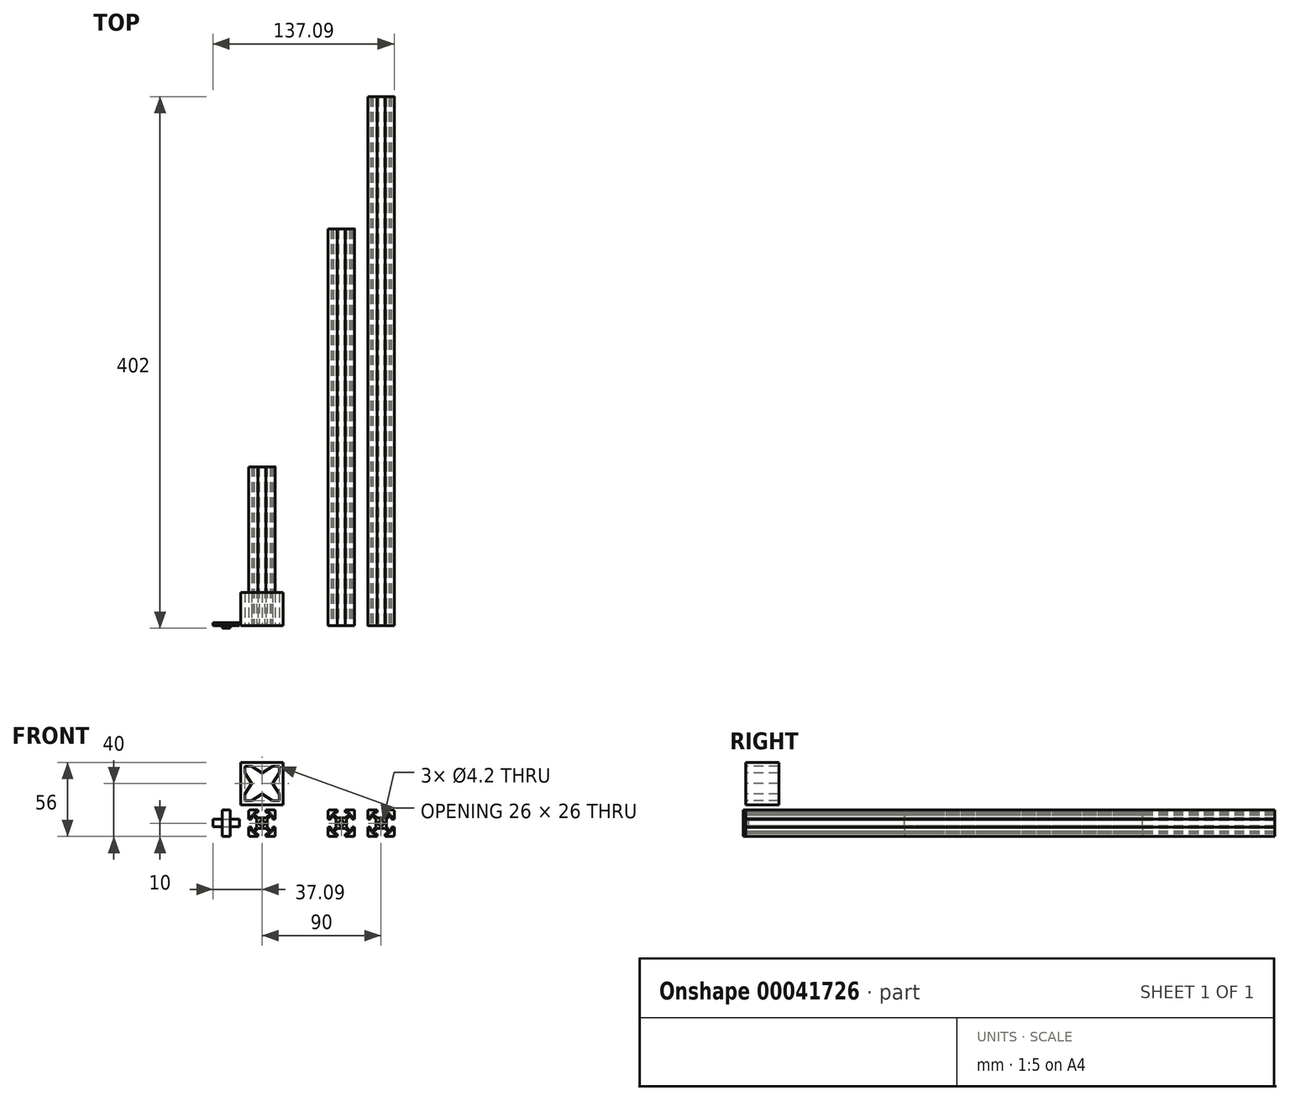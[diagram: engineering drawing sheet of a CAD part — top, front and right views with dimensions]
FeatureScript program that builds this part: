
annotation { "Feature Type Name" : "Feature", "Feature Type Description" : "" }
export const myFeature = defineFeature(function(context is Context, id is Id, definition is map)
    precondition{}
    {
        {
            var Q0;
            Q0=qCreatedBy(makeId("Front.planeOp"),FACE);
            var sketch = newSketch(context, id + "F0", { "sketchPlane" : qUnion([Q0])});
            skLineSegment(sketch, "E0", {"start": v(0, 4) * mm, "end": v(3, 4) * mm});
            skLineSegment(sketch, "E1", {"start": v(3, 4) * mm, "end": v(6, 7) * mm});
            skLineSegment(sketch, "E2", {"start": v(6, 7) * mm, "end": v(6, 8) * mm});
            skLineSegment(sketch, "E3", {"start": v(6, 8) * mm, "end": v(3, 8) * mm});
            skLineSegment(sketch, "E4", {"start": v(3, 8) * mm, "end": v(3, 10) * mm});
            skLineSegment(sketch, "E5", {"start": v(3, 10) * mm, "end": v(9, 10) * mm});
            skLineSegment(sketch, "E6", {"start": v(0, 0) * mm, "end": v(12.93, 12.93) * mm, "construction": true});
            skLineSegment(sketch, "E7.MirrorCS", {"start": v(4, 0) * mm, "end": v(4, 3) * mm});
            skLineSegment(sketch, "E8.MirrorCS", {"start": v(10, 3) * mm, "end": v(10, 9) * mm});
            skLineSegment(sketch, "E9.MirrorCS", {"start": v(8, 3) * mm, "end": v(10, 3) * mm});
            skLineSegment(sketch, "E10.MirrorCS", {"start": v(8, 6) * mm, "end": v(8, 3) * mm});
            skLineSegment(sketch, "E11.MirrorCS", {"start": v(4, 3) * mm, "end": v(7, 6) * mm});
            skLineSegment(sketch, "E12.MirrorCS", {"start": v(7, 6) * mm, "end": v(8, 6) * mm});
            skLineSegment(sketch, "E13.MirrorCS", {"start": v(-8, 3) * mm, "end": v(-10, 3) * mm});
            skLineSegment(sketch, "E14.MirrorCS", {"start": v(0, 4) * mm, "end": v(-3, 4) * mm});
            skLineSegment(sketch, "E15.MirrorCS", {"start": v(-3, 4) * mm, "end": v(-6, 7) * mm});
            skLineSegment(sketch, "E16.MirrorCS", {"start": v(-6, 7) * mm, "end": v(-6, 8) * mm});
            skLineSegment(sketch, "E17.MirrorCS", {"start": v(-6, 8) * mm, "end": v(-3, 8) * mm});
            skLineSegment(sketch, "E18.MirrorCS", {"start": v(-3, 8) * mm, "end": v(-3, 10) * mm});
            skLineSegment(sketch, "E19.MirrorCS", {"start": v(-3, 10) * mm, "end": v(-9, 10) * mm});
            skLineSegment(sketch, "E20.MirrorCS", {"start": v(-4, 0) * mm, "end": v(-4, 3) * mm});
            skLineSegment(sketch, "E21.MirrorCS", {"start": v(-10, 3) * mm, "end": v(-10, 9) * mm});
            skLineSegment(sketch, "E22.MirrorCS", {"start": v(-8, 6) * mm, "end": v(-8, 3) * mm});
            skLineSegment(sketch, "E23.MirrorCS", {"start": v(-4, 3) * mm, "end": v(-7, 6) * mm});
            skLineSegment(sketch, "E24.MirrorCS", {"start": v(-7, 6) * mm, "end": v(-8, 6) * mm});
            skLineSegment(sketch, "E25.MirrorCS", {"start": v(-7, -6) * mm, "end": v(-8, -6) * mm});
            skLineSegment(sketch, "E26.MirrorCS", {"start": v(-6, -7) * mm, "end": v(-6, -8) * mm});
            skLineSegment(sketch, "E27.MirrorCS", {"start": v(6, -7) * mm, "end": v(6, -8) * mm});
            skLineSegment(sketch, "E28.MirrorCS", {"start": v(7, -6) * mm, "end": v(8, -6) * mm});
            skLineSegment(sketch, "E29.MirrorCS", {"start": v(8, -3) * mm, "end": v(10, -3) * mm});
            skLineSegment(sketch, "E30.MirrorCS", {"start": v(-8, -3) * mm, "end": v(-10, -3) * mm});
            skLineSegment(sketch, "E31.MirrorCS", {"start": v(-6, -8) * mm, "end": v(-3, -8) * mm});
            skLineSegment(sketch, "E32.MirrorCS", {"start": v(-3, -10) * mm, "end": v(-9, -10) * mm});
            skLineSegment(sketch, "E33.MirrorCS", {"start": v(-4, -3) * mm, "end": v(-7, -6) * mm});
            skLineSegment(sketch, "E34.MirrorCS", {"start": v(-4, 0) * mm, "end": v(-4, -3) * mm});
            skLineSegment(sketch, "E35.MirrorCS", {"start": v(-3, -8) * mm, "end": v(-3, -10) * mm});
            skLineSegment(sketch, "E36.MirrorCS", {"start": v(0, -4) * mm, "end": v(-3, -4) * mm});
            skLineSegment(sketch, "E37.MirrorCS", {"start": v(0, -4) * mm, "end": v(3, -4) * mm});
            skLineSegment(sketch, "E38.MirrorCS", {"start": v(6, -8) * mm, "end": v(3, -8) * mm});
            skLineSegment(sketch, "E39.MirrorCS", {"start": v(3, -8) * mm, "end": v(3, -10) * mm});
            skLineSegment(sketch, "E40.MirrorCS", {"start": v(3, -10) * mm, "end": v(9, -10) * mm});
            skLineSegment(sketch, "E41.MirrorCS", {"start": v(3, -4) * mm, "end": v(6, -7) * mm});
            skLineSegment(sketch, "E42.MirrorCS", {"start": v(-3, -4) * mm, "end": v(-6, -7) * mm});
            skLineSegment(sketch, "E43.MirrorCS", {"start": v(4, 0) * mm, "end": v(4, -3) * mm});
            skLineSegment(sketch, "E44.MirrorCS", {"start": v(10, -3) * mm, "end": v(10, -9) * mm});
            skLineSegment(sketch, "E45.MirrorCS", {"start": v(8, -6) * mm, "end": v(8, -3) * mm});
            skLineSegment(sketch, "E46.MirrorCS", {"start": v(4, -3) * mm, "end": v(7, -6) * mm});
            skLineSegment(sketch, "E47.MirrorCS", {"start": v(-8, -6) * mm, "end": v(-8, -3) * mm});
            skLineSegment(sketch, "E48.MirrorCS", {"start": v(-10, -3) * mm, "end": v(-10, -9) * mm});
            skCircle(sketch, "E49", {"center": v(0, 0) * mm, "radius": 2.1 * mm});
            skPoint(sketch, "E50.visualSharp", {"position": v(-10, 10) * mm});
            skArc(sketch, "E50.filletArc", {"start": v(-9, 10) * mm, "mid": v(-9.7, 9.7) * mm, "end": v(-10, 9) * mm});
            skPoint(sketch, "E51.visualSharp", {"position": v(10, 10) * mm});
            skArc(sketch, "E51.filletArc", {"start": v(10, 9) * mm, "mid": v(9.7, 9.7) * mm, "end": v(9, 10) * mm});
            skPoint(sketch, "E52.visualSharp", {"position": v(10, -10) * mm});
            skArc(sketch, "E52.filletArc", {"start": v(9, -10) * mm, "mid": v(9.7, -9.7) * mm, "end": v(10, -9) * mm});
            skPoint(sketch, "E53.visualSharp", {"position": v(-10, -10) * mm});
            skArc(sketch, "E53.filletArc", {"start": v(-10, -9) * mm, "mid": v(-9.7, -9.7) * mm, "end": v(-9, -10) * mm});
            skLineSegment(sketch, "E54", {"start": v(-3, 4) * mm, "end": v(-3, 8) * mm, "construction": true});
            skLineSegment(sketch, "E55", {"start": v(3, 4) * mm, "end": v(3, 8) * mm, "construction": true});
            skSolve(sketch);
        }
        {
            var Q0;
            Q0=makeQuery(id+"F0.imprint","IMPRINT",FACE,{"disambiguationData":[TD([[makeQuery(id+"F0.imprint","IMPRINT",EDGE,{"derivedFrom":sQuery(id+"F0.wireOp",EDGE,"E0")}),-1.0]])]});
            extrude(context, id + "F1", {"entities" : qUnion([Q0]), "oppositeDirection" : true, "depth" : 120 * mm});
        }
        {
            var Q0;
            Q0=makeQuery(id+"F0.imprint","IMPRINT",FACE,{"disambiguationData":[TD([[makeQuery(id+"F0.imprint","IMPRINT",EDGE,{"derivedFrom":sQuery(id+"F0.wireOp",EDGE,"E0")}),-1.0]])]});
            var sketch = newSketch(context, id + "F2", { "sketchPlane" : qUnion([Q0])});
            skLineSegment(sketch, "E56.0", {"start": v(0, 0) * mm, "end": v(12.93, 12.93) * mm, "construction": true});
            skLineSegment(sketch, "E57", {"start": v(13, 13) * mm, "end": v(7.97, 13) * mm});
            skLineSegment(sketch, "E58", {"start": v(7.97, 13) * mm, "end": v(0, 8) * mm});
            skLineSegment(sketch, "E59.MirrorCS", {"start": v(13, 13) * mm, "end": v(13, 7.97) * mm});
            skLineSegment(sketch, "E60.MirrorCS", {"start": v(13, 7.97) * mm, "end": v(8, 0) * mm});
            skLineSegment(sketch, "E61.MirrorCS", {"start": v(-7.97, 13) * mm, "end": v(0, 8) * mm});
            skLineSegment(sketch, "E62.MirrorCS", {"start": v(-13, 13) * mm, "end": v(-7.97, 13) * mm});
            skLineSegment(sketch, "E63.MirrorCS", {"start": v(-13, 7.97) * mm, "end": v(-8, 0) * mm});
            skLineSegment(sketch, "E64.MirrorCS", {"start": v(-13, 13) * mm, "end": v(-13, 7.97) * mm});
            skLineSegment(sketch, "E65.MirrorCS", {"start": v(-7.97, -13) * mm, "end": v(0, -8) * mm});
            skLineSegment(sketch, "E66.MirrorCS", {"start": v(-13, -13) * mm, "end": v(-7.97, -13) * mm});
            skLineSegment(sketch, "E67.MirrorCS", {"start": v(7.97, -13) * mm, "end": v(0, -8) * mm});
            skLineSegment(sketch, "E68.MirrorCS", {"start": v(-13, -7.97) * mm, "end": v(-8, 0) * mm});
            skLineSegment(sketch, "E69.MirrorCS", {"start": v(-13, -13) * mm, "end": v(-13, -7.97) * mm});
            skLineSegment(sketch, "E70.MirrorCS", {"start": v(13, -13) * mm, "end": v(7.97, -13) * mm});
            skLineSegment(sketch, "E71.MirrorCS", {"start": v(13, -13) * mm, "end": v(13, -7.97) * mm});
            skLineSegment(sketch, "E72.MirrorCS", {"start": v(13, -7.97) * mm, "end": v(8, 0) * mm});
            skLineSegment(sketch, "E73.rect.bottom", {"start": v(-16, 16) * mm, "end": v(16, 16) * mm});
            skLineSegment(sketch, "E73.rect.top", {"start": v(-16, -16) * mm, "end": v(16, -16) * mm});
            skLineSegment(sketch, "E73.rect.left", {"start": v(-16, 16) * mm, "end": v(-16, -16) * mm});
            skLineSegment(sketch, "E73.rect.right", {"start": v(16, 16) * mm, "end": v(16, -16) * mm});
            skPoint(sketch, "E73.rect.middle", {"position": v(0, 0) * mm});
            skSolve(sketch);
        }
        {
            var Q0;
            Q0=qSketchRegion(id+"F0",true);
            extrude(context, id + "F3", {"entities" : qUnion([Q0]), "oppositeDirection" : true, "depth" : 300 * mm});
        }
        {
            var Q0;
            Q0=qSketchRegion(id+"F0",true);
            extrude(context, id + "F4", {"entities" : qUnion([Q0]), "oppositeDirection" : true, "depth" : 400 * mm});
        }
        {
            var Q0;
            Q0=makeQuery(id+"F3.opExtrude","SWEPT_BODY",BODY,{"disambiguationData":[OSD([sQuery(id+"F0.wireOp",EDGE,"E0"),sQuery(id+"F0.wireOp",EDGE,"E1"),sQuery(id+"F0.wireOp",EDGE,"E2"),sQuery(id+"F0.wireOp",EDGE,"E3"),sQuery(id+"F0.wireOp",EDGE,"E4"),sQuery(id+"F0.wireOp",EDGE,"E5"),sQuery(id+"F0.wireOp",EDGE,"E7.MirrorCS"),sQuery(id+"F0.wireOp",EDGE,"E8.MirrorCS"),sQuery(id+"F0.wireOp",EDGE,"E10.MirrorCS"),sQuery(id+"F0.wireOp",EDGE,"E11.MirrorCS"),sQuery(id+"F0.wireOp",EDGE,"E12.MirrorCS"),sQuery(id+"F0.wireOp",EDGE,"E9.MirrorCS"),sQuery(id+"F0.wireOp",EDGE,"E14.MirrorCS"),sQuery(id+"F0.wireOp",EDGE,"E15.MirrorCS"),sQuery(id+"F0.wireOp",EDGE,"E16.MirrorCS"),sQuery(id+"F0.wireOp",EDGE,"E17.MirrorCS"),sQuery(id+"F0.wireOp",EDGE,"E18.MirrorCS"),sQuery(id+"F0.wireOp",EDGE,"E19.MirrorCS"),sQuery(id+"F0.wireOp",EDGE,"E20.MirrorCS"),sQuery(id+"F0.wireOp",EDGE,"E21.MirrorCS"),sQuery(id+"F0.wireOp",EDGE,"E22.MirrorCS"),sQuery(id+"F0.wireOp",EDGE,"E23.MirrorCS"),sQuery(id+"F0.wireOp",EDGE,"E13.MirrorCS"),sQuery(id+"F0.wireOp",EDGE,"E24.MirrorCS"),sQuery(id+"F0.wireOp",EDGE,"E25.MirrorCS"),sQuery(id+"F0.wireOp",EDGE,"E26.MirrorCS"),sQuery(id+"F0.wireOp",EDGE,"E27.MirrorCS"),sQuery(id+"F0.wireOp",EDGE,"E28.MirrorCS"),sQuery(id+"F0.wireOp",EDGE,"E31.MirrorCS"),sQuery(id+"F0.wireOp",EDGE,"E32.MirrorCS"),sQuery(id+"F0.wireOp",EDGE,"E33.MirrorCS"),sQuery(id+"F0.wireOp",EDGE,"E34.MirrorCS"),sQuery(id+"F0.wireOp",EDGE,"E35.MirrorCS"),sQuery(id+"F0.wireOp",EDGE,"E36.MirrorCS"),sQuery(id+"F0.wireOp",EDGE,"E37.MirrorCS"),sQuery(id+"F0.wireOp",EDGE,"E38.MirrorCS"),sQuery(id+"F0.wireOp",EDGE,"E39.MirrorCS"),sQuery(id+"F0.wireOp",EDGE,"E40.MirrorCS"),sQuery(id+"F0.wireOp",EDGE,"E41.MirrorCS"),sQuery(id+"F0.wireOp",EDGE,"E42.MirrorCS"),sQuery(id+"F0.wireOp",EDGE,"E43.MirrorCS"),sQuery(id+"F0.wireOp",EDGE,"E44.MirrorCS"),sQuery(id+"F0.wireOp",EDGE,"E29.MirrorCS"),sQuery(id+"F0.wireOp",EDGE,"E45.MirrorCS"),sQuery(id+"F0.wireOp",EDGE,"E46.MirrorCS"),sQuery(id+"F0.wireOp",EDGE,"E47.MirrorCS"),sQuery(id+"F0.wireOp",EDGE,"E48.MirrorCS"),sQuery(id+"F0.wireOp",EDGE,"E30.MirrorCS"),sQuery(id+"F0.wireOp",EDGE,"E49"),sQuery(id+"F0.wireOp",EDGE,"E50.filletArc"),sQuery(id+"F0.wireOp",EDGE,"E51.filletArc"),sQuery(id+"F0.wireOp",EDGE,"E52.filletArc"),sQuery(id+"F0.wireOp",EDGE,"E53.filletArc")])]});
            transform(context, id + "F5", {"entities" : qUnion([Q0]), "transformType" : TransformType.TRANSLATION_3D, "dx" : 60 * mm, "dy" : 0 * mm, "dz" : 0 * mm, "makeCopy" : false});
        }
        {
            var Q0;
            Q0=makeQuery(id+"F4.opExtrude","SWEPT_BODY",BODY,{"disambiguationData":[OSD([sQuery(id+"F0.wireOp",EDGE,"E0"),sQuery(id+"F0.wireOp",EDGE,"E1"),sQuery(id+"F0.wireOp",EDGE,"E2"),sQuery(id+"F0.wireOp",EDGE,"E3"),sQuery(id+"F0.wireOp",EDGE,"E4"),sQuery(id+"F0.wireOp",EDGE,"E5"),sQuery(id+"F0.wireOp",EDGE,"E7.MirrorCS"),sQuery(id+"F0.wireOp",EDGE,"E8.MirrorCS"),sQuery(id+"F0.wireOp",EDGE,"E10.MirrorCS"),sQuery(id+"F0.wireOp",EDGE,"E11.MirrorCS"),sQuery(id+"F0.wireOp",EDGE,"E12.MirrorCS"),sQuery(id+"F0.wireOp",EDGE,"E9.MirrorCS"),sQuery(id+"F0.wireOp",EDGE,"E14.MirrorCS"),sQuery(id+"F0.wireOp",EDGE,"E15.MirrorCS"),sQuery(id+"F0.wireOp",EDGE,"E16.MirrorCS"),sQuery(id+"F0.wireOp",EDGE,"E17.MirrorCS"),sQuery(id+"F0.wireOp",EDGE,"E18.MirrorCS"),sQuery(id+"F0.wireOp",EDGE,"E19.MirrorCS"),sQuery(id+"F0.wireOp",EDGE,"E20.MirrorCS"),sQuery(id+"F0.wireOp",EDGE,"E21.MirrorCS"),sQuery(id+"F0.wireOp",EDGE,"E22.MirrorCS"),sQuery(id+"F0.wireOp",EDGE,"E23.MirrorCS"),sQuery(id+"F0.wireOp",EDGE,"E13.MirrorCS"),sQuery(id+"F0.wireOp",EDGE,"E24.MirrorCS"),sQuery(id+"F0.wireOp",EDGE,"E25.MirrorCS"),sQuery(id+"F0.wireOp",EDGE,"E26.MirrorCS"),sQuery(id+"F0.wireOp",EDGE,"E27.MirrorCS"),sQuery(id+"F0.wireOp",EDGE,"E28.MirrorCS"),sQuery(id+"F0.wireOp",EDGE,"E31.MirrorCS"),sQuery(id+"F0.wireOp",EDGE,"E32.MirrorCS"),sQuery(id+"F0.wireOp",EDGE,"E33.MirrorCS"),sQuery(id+"F0.wireOp",EDGE,"E34.MirrorCS"),sQuery(id+"F0.wireOp",EDGE,"E35.MirrorCS"),sQuery(id+"F0.wireOp",EDGE,"E36.MirrorCS"),sQuery(id+"F0.wireOp",EDGE,"E37.MirrorCS"),sQuery(id+"F0.wireOp",EDGE,"E38.MirrorCS"),sQuery(id+"F0.wireOp",EDGE,"E39.MirrorCS"),sQuery(id+"F0.wireOp",EDGE,"E40.MirrorCS"),sQuery(id+"F0.wireOp",EDGE,"E41.MirrorCS"),sQuery(id+"F0.wireOp",EDGE,"E42.MirrorCS"),sQuery(id+"F0.wireOp",EDGE,"E43.MirrorCS"),sQuery(id+"F0.wireOp",EDGE,"E44.MirrorCS"),sQuery(id+"F0.wireOp",EDGE,"E29.MirrorCS"),sQuery(id+"F0.wireOp",EDGE,"E45.MirrorCS"),sQuery(id+"F0.wireOp",EDGE,"E46.MirrorCS"),sQuery(id+"F0.wireOp",EDGE,"E47.MirrorCS"),sQuery(id+"F0.wireOp",EDGE,"E48.MirrorCS"),sQuery(id+"F0.wireOp",EDGE,"E30.MirrorCS"),sQuery(id+"F0.wireOp",EDGE,"E49"),sQuery(id+"F0.wireOp",EDGE,"E50.filletArc"),sQuery(id+"F0.wireOp",EDGE,"E51.filletArc"),sQuery(id+"F0.wireOp",EDGE,"E52.filletArc"),sQuery(id+"F0.wireOp",EDGE,"E53.filletArc")])]});
            transform(context, id + "F6", {"entities" : qUnion([Q0]), "transformType" : TransformType.TRANSLATION_3D, "dx" : 90 * mm, "dy" : 0 * mm, "dz" : 0 * mm, "makeCopy" : false});
        }
        {
            var Q0;
            Q0=qCreatedBy(makeId("Front.planeOp"),FACE);
            var sketch = newSketch(context, id + "F7", { "sketchPlane" : qUnion([Q0])});
            skLineSegment(sketch, "E74.bottom", {"start": v(-37.1, 10.2) * mm, "end": v(-17.1, 10.2) * mm});
            skLineSegment(sketch, "E74.top", {"start": v(-37.1, -9.8) * mm, "end": v(-17.1, -9.8) * mm});
            skLineSegment(sketch, "E74.left", {"start": v(-37.1, 10.2) * mm, "end": v(-37.1, -9.8) * mm});
            skLineSegment(sketch, "E74.right", {"start": v(-17.1, 10.2) * mm, "end": v(-17.1, -9.8) * mm});
            skLineSegment(sketch, "E75", {"start": v(-30.1, 10.2) * mm, "end": v(-30.1, -9.8) * mm});
            skLineSegment(sketch, "E76", {"start": v(-24.1, 10.2) * mm, "end": v(-24.1, -9.8) * mm});
            skLineSegment(sketch, "E77", {"start": v(-37.1, -2.8) * mm, "end": v(-17.1, -2.8) * mm});
            skLineSegment(sketch, "E78", {"start": v(-37.1, 3.2) * mm, "end": v(-17.1, 3.2) * mm});
            skLineSegment(sketch, "E79", {"start": v(-30.1, 3.2) * mm, "end": v(-24.1, -2.8) * mm, "construction": true});
            skLineSegment(sketch, "E80", {"start": v(-24.1, 3.2) * mm, "end": v(-30.1, -2.8) * mm, "construction": true});
            skPoint(sketch, "E81", {"position": v(-27.1, 0.2) * mm});
            skSolve(sketch);
        }
        {
            var Q0;
            {var subQ3=sQuery(id+"F7.wireOp",EDGE,"E75");var subQ5=sQuery(id+"F7.wireOp",EDGE,"E74.bottom");var subQ7=makeQuery(id+"F7.imprint","INTERSECT",VERTEX,{"derivedFrom":[subQ5,subQ3]});Q0=makeQuery(id+"F7.imprint","IMPRINT",FACE,{"disambiguationData":[TD([[makeQuery(id+"F7.imprint","IMPRINT",EDGE,{"disambiguationData":[TD([[subQ7,-1.0]])],"derivedFrom":subQ5}),-1.0]])]});}
            var Q1;
            {var subQ0=sQuery(id+"F7.wireOp",EDGE,"E78");var subQ3=sQuery(id+"F7.wireOp",EDGE,"E75");var subQ4=makeQuery(id+"F7.imprint","INTERSECT",VERTEX,{"derivedFrom":[subQ3,subQ0]});Q1=makeQuery(id+"F7.imprint","IMPRINT",FACE,{"disambiguationData":[TD([[makeQuery(id+"F7.imprint","IMPRINT",EDGE,{"disambiguationData":[TD([[subQ4,-1.0]])],"derivedFrom":subQ3}),1.0]])]});}
            var Q2;
            {var subQ3=sQuery(id+"F7.wireOp",EDGE,"E75");var subQ5=sQuery(id+"F7.wireOp",EDGE,"E74.top");var subQ7=makeQuery(id+"F7.imprint","INTERSECT",VERTEX,{"derivedFrom":[subQ5,subQ3]});Q2=makeQuery(id+"F7.imprint","IMPRINT",FACE,{"disambiguationData":[TD([[makeQuery(id+"F7.imprint","IMPRINT",EDGE,{"disambiguationData":[TD([[subQ7,-1.0]])],"derivedFrom":subQ5}),1.0]])]});}
            extrude(context, id + "F8", {"entities" : qUnion([Q0, Q1, Q2]), "depth" : 2 * mm});
        }
        {
            var Q0;
            {var subQ3=sQuery(id+"F7.wireOp",EDGE,"E74.left");var subQ5=sQuery(id+"F7.wireOp",EDGE,"E77");var subQ7=makeQuery(id+"F7.imprint","INTERSECT",VERTEX,{"derivedFrom":[subQ3,subQ5]});Q0=makeQuery(id+"F7.imprint","IMPRINT",FACE,{"disambiguationData":[TD([[makeQuery(id+"F7.imprint","IMPRINT",EDGE,{"disambiguationData":[TD([[subQ7,1.0]])],"derivedFrom":subQ3}),1.0]])]});}
            var Q1;
            {var subQ0=sQuery(id+"F7.wireOp",EDGE,"E78");var subQ3=sQuery(id+"F7.wireOp",EDGE,"E75");var subQ4=makeQuery(id+"F7.imprint","INTERSECT",VERTEX,{"derivedFrom":[subQ3,subQ0]});Q1=makeQuery(id+"F7.imprint","IMPRINT",FACE,{"disambiguationData":[TD([[makeQuery(id+"F7.imprint","IMPRINT",EDGE,{"disambiguationData":[TD([[subQ4,-1.0]])],"derivedFrom":subQ3}),1.0]])]});}
            var Q2;
            {var subQ3=sQuery(id+"F7.wireOp",EDGE,"E74.right");var subQ5=sQuery(id+"F7.wireOp",EDGE,"E77");var subQ7=makeQuery(id+"F7.imprint","INTERSECT",VERTEX,{"derivedFrom":[subQ3,subQ5]});Q2=makeQuery(id+"F7.imprint","IMPRINT",FACE,{"disambiguationData":[TD([[makeQuery(id+"F7.imprint","IMPRINT",EDGE,{"disambiguationData":[TD([[subQ7,1.0]])],"derivedFrom":subQ3}),-1.0]])]});}
            extrude(context, id + "F9", {"entities" : qUnion([Q0, Q1, Q2]), "operationType" : NewBodyOperationType.ADD, "oppositeDirection" : true, "depth" : 2 * mm});
        }
        {
            var Q0;
            Q0=makeQuery(id+"F3.opExtrude","SWEPT_FACE",FACE,{"disambiguationData":[OSD([sQuery(id+"F0.wireOp",EDGE,"E5")])]});
            var sketch = newSketch(context, id + "F10", { "sketchPlane" : qUnion([Q0])});
            skLineSegment(sketch, "E82.0", {"start": v(50, 300) * mm, "end": v(50, 0) * mm, "construction": true});
            skLineSegment(sketch, "E83.1", {"start": v(70, 300) * mm, "end": v(70, 0) * mm, "construction": true});
            skLineSegment(sketch, "E84", {"start": v(50, 150) * mm, "end": v(70, 150) * mm, "construction": true});
            skPoint(sketch, "E85", {"position": v(60, 150) * mm});
            skPoint(sketch, "E86", {"position": v(33.74, 152.67) * mm});
            skLineSegment(sketch, "E87", {"start": v(60, 70) * mm, "end": v(60, 230) * mm, "construction": true});
            skPoint(sketch, "E88", {"position": v(60, 70) * mm});
            skPoint(sketch, "E89", {"position": v(60, 230) * mm});
            skPoint(sketch, "E90", {"position": v(27.74, 198.96) * mm});
            skSolve(sketch);
        }
        {
            var Q0;
            {var subQ52=sQuery(id+"F2.wireOp",EDGE,"E57");Q0=makeQuery(id+"F2.imprint","IMPRINT",FACE,{"disambiguationData":[TD([[makeQuery(id+"F2.imprint","IMPRINT",EDGE,{"derivedFrom":subQ52}),-1.0]])]});}
            var Q1;
            Q1=qSketchRegion(id+"F2",true);
            extrude(context, id + "F11", {"entities" : qUnion([Q0, Q1]), "oppositeDirection" : true, "depth" : 25 * mm});
        }
        {
            var Q0;
            Q0=makeQuery(id+"F11.opExtrude","SWEPT_BODY",BODY,{"disambiguationData":[OSD([sQuery(id+"F2.wireOp",EDGE,"E57"),sQuery(id+"F2.wireOp",EDGE,"E58"),sQuery(id+"F2.wireOp",EDGE,"E59.MirrorCS"),sQuery(id+"F2.wireOp",EDGE,"E60.MirrorCS"),sQuery(id+"F2.wireOp",EDGE,"E61.MirrorCS"),sQuery(id+"F2.wireOp",EDGE,"E62.MirrorCS"),sQuery(id+"F2.wireOp",EDGE,"E63.MirrorCS"),sQuery(id+"F2.wireOp",EDGE,"E64.MirrorCS"),sQuery(id+"F2.wireOp",EDGE,"E65.MirrorCS"),sQuery(id+"F2.wireOp",EDGE,"E66.MirrorCS"),sQuery(id+"F2.wireOp",EDGE,"E67.MirrorCS"),sQuery(id+"F2.wireOp",EDGE,"E68.MirrorCS"),sQuery(id+"F2.wireOp",EDGE,"E69.MirrorCS"),sQuery(id+"F2.wireOp",EDGE,"E70.MirrorCS"),sQuery(id+"F2.wireOp",EDGE,"E71.MirrorCS"),sQuery(id+"F2.wireOp",EDGE,"E72.MirrorCS"),sQuery(id+"F2.wireOp",EDGE,"E73.rect.bottom"),sQuery(id+"F2.wireOp",EDGE,"E73.rect.top"),sQuery(id+"F2.wireOp",EDGE,"E73.rect.left"),sQuery(id+"F2.wireOp",EDGE,"E73.rect.right")])]});
            transform(context, id + "F12", {"entities" : qUnion([Q0]), "transformType" : TransformType.TRANSLATION_3D, "dx" : 0 * mm, "dy" : 0 * mm, "dz" : 30 * mm, "makeCopy" : false});
        }
    });
